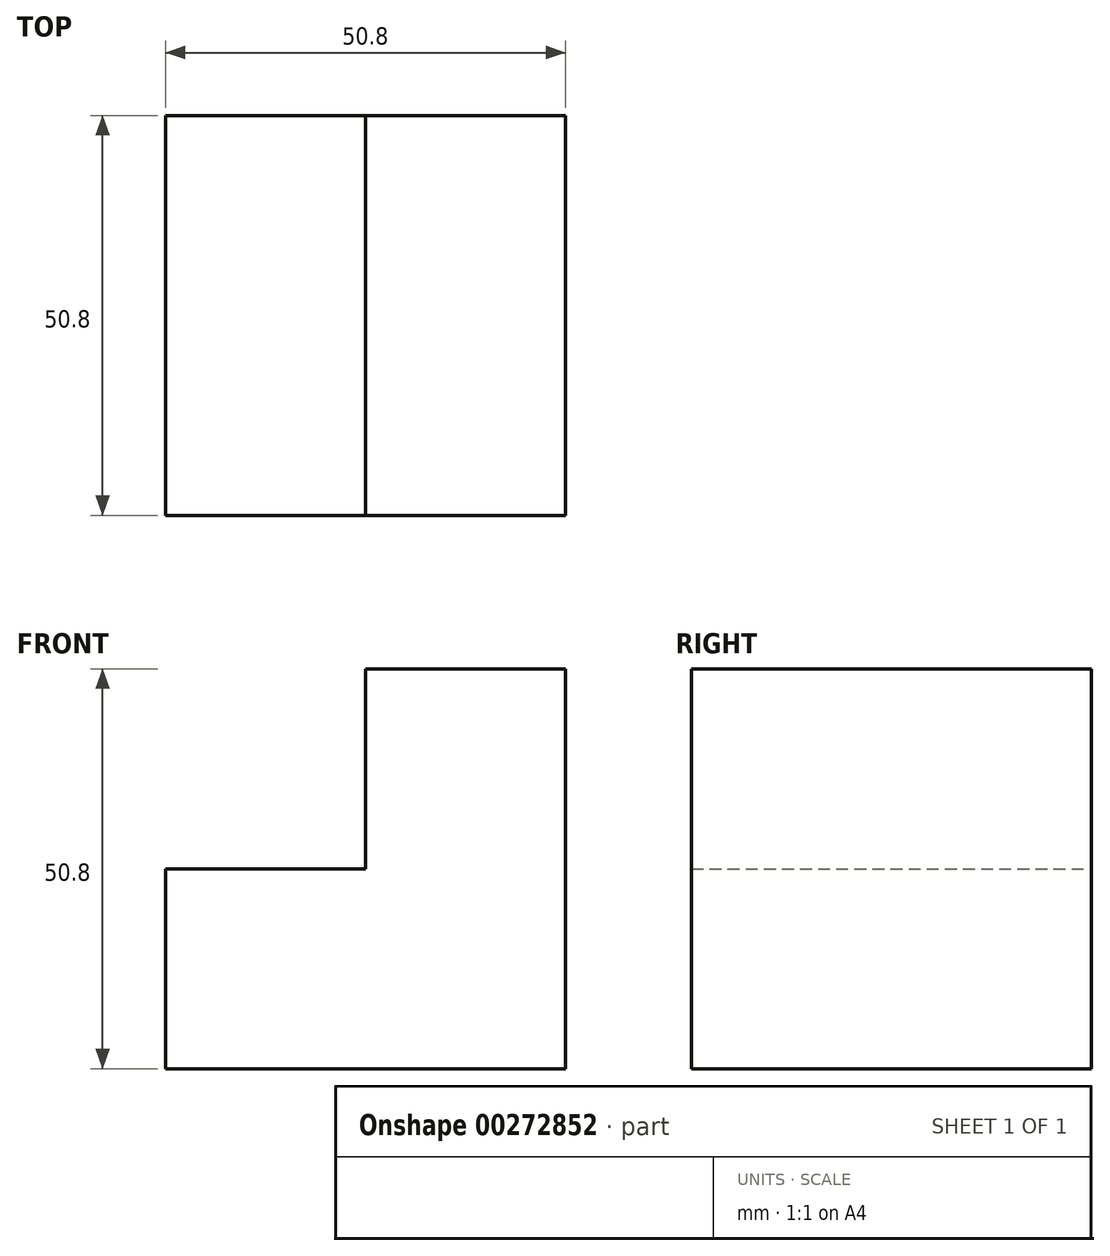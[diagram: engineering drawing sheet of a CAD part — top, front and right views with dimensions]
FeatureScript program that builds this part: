
annotation { "Feature Type Name" : "Feature", "Feature Type Description" : "" }
export const myFeature = defineFeature(function(context is Context, id is Id, definition is map)
    precondition{}
    {
        {
            var Q0;
            Q0=qCreatedBy(makeId("Front.planeOp"),FACE);
            var sketch = newSketch(context, id + "F0", { "sketchPlane" : qUnion([Q0])});
            skLineSegment(sketch, "E0", {"start": v(0, 0) * mm, "end": v(0, 50.8) * mm});
            skLineSegment(sketch, "E1", {"start": v(0, 0) * mm, "end": v(-50.8, 0) * mm});
            skLineSegment(sketch, "E2", {"start": v(0, 50.8) * mm, "end": v(-25.4, 50.8) * mm});
            skLineSegment(sketch, "E3", {"start": v(-50.8, 0) * mm, "end": v(-50.8, 25.4) * mm});
            skLineSegment(sketch, "E4", {"start": v(-50.8, 25.4) * mm, "end": v(-25.4, 25.4) * mm});
            skLineSegment(sketch, "E5", {"start": v(-25.4, 50.8) * mm, "end": v(-25.4, 25.4) * mm});
            skSolve(sketch);
        }
        {
            var Q0;
            Q0 = qSketchRegion(id + "F0", true);
            extrude(context, id + "F1", {"entities" : qUnion([Q0]), "depth" : 50.8 * mm});
        }
    });
